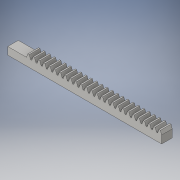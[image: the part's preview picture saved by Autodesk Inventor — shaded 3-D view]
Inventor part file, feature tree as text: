
AUTODESK INVENTOR PART (.ipt)
format: ipt  version: 2016 (Build 200138000, 138)  size: 282,624 bytes
history: native  units: in
note: dims shown in document units (in); Inventor stores cm internally (conversion verified against a paired STEP export)
features: extrude x1, sketch x1
ambient origin geometry x8: Origin, YZ Plane, XZ Plane, XY Plane, X Axis, Y Axis, Z Axis, Center Point
bodies: Solid1 (feature_tree)
feature tree (2):
  extrude  "Extrusion1"  Depth=0.5in
  sketch  "Sketch1"  dims[d0=0.5in d1=0.0in d4=0.0245in d5=0.0122in]
